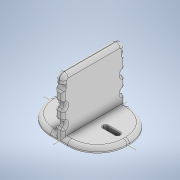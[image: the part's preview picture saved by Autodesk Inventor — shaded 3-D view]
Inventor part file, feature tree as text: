
AUTODESK INVENTOR PART (.ipt)
format: ipt  version: 2021 (Build 250183000, 183)  size: 360,448 bytes
history: native  units: mm
features: fillet x8, extrude x4, sketch x4
ambient origin geometry x8: Origin, YZ Plane, XZ Plane, XY Plane, X Axis, Y Axis, Z Axis, Center Point
bodies: Solid1 (feature_tree)
feature tree (16):
  extrude  "Extrusion1"  Depth=50.0mm
  extrude  "Extrusion2"  Depth=25.0mm
  extrude  "Extrusion3"  Depth=3.2mm
  fillet  "Fillet2"  Radius=3.2mm
  fillet  "Fillet3"  Radius=43.0mm
  fillet  "Fillet4"  Radius=11.0mm
  fillet  "Fillet5"  Radius=11.0mm
  fillet  "Fillet6"  Radius=13.0mm
  extrude  "Extrusion4"  Depth=2.0mm
  fillet  "Fillet7"  Radius=3.5mm
  fillet  "Fillet8"  Radius=1.75mm
  fillet  "Fillet9"  Radius=43.0mm
  sketch  "Sketch1"  dims[d0=62.0mm d1=50.0mm]
  sketch  "Sketch2"  dims[d2=31.0mm d3=25.0mm]
  sketch  "Sketch3"  dims[d4=4.0mm d5=0.0mm d6=3.2mm d7=3.2mm d8=43.0mm d9=0.0mm d11=11.0mm d12=11.0mm d13=13.0mm]
  sketch  "Sketch4"  dims[d14=13.0mm d15=3.5mm d16=3.5mm d17=1.75mm d18=43.0mm d19=0.0mm d20=1.5mm d21=0.6mm d22=24.0mm d23=4.0mm d24=3.0mm d25=5.0mm d26=5.0mm d27=5.0mm d29=12.0mm d30=13.0mm d31=13.0mm d32=5.0mm d33=5.0mm d34=5.0mm d35=13.0mm d36=13.0mm d37=5.0mm d38=0.0mm d39=3.0mm d40=2.0mm d41=2.0mm]
